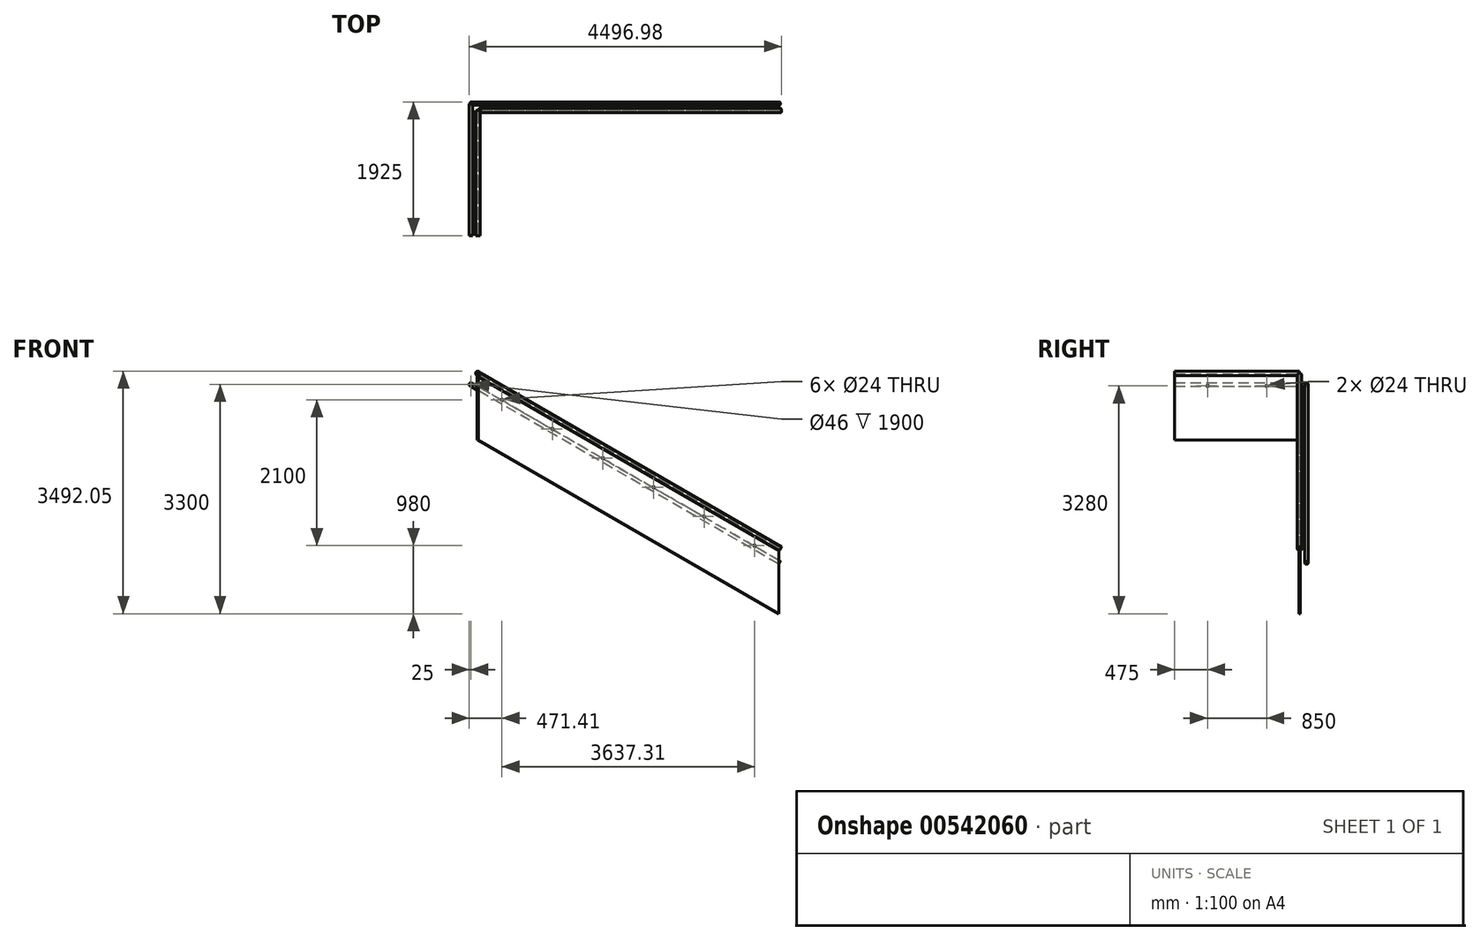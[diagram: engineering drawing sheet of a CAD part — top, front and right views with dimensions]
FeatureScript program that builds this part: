
annotation { "Feature Type Name" : "Feature", "Feature Type Description" : "" }
export const myFeature = defineFeature(function(context is Context, id is Id, definition is map)
    precondition{}
    {
        {
            var Q0;
            Q0=qCreatedBy(makeId("Front.planeOp"),FACE);
            var sketch = newSketch(context, id + "F0", { "sketchPlane" : qUnion([Q0])});
            skLineSegment(sketch, "E0", {"start": v(0, 0) * mm, "end": v(4330.13, -2500) * mm});
            skLineSegment(sketch, "E1", {"start": v(4330.13, -2500) * mm, "end": v(4330.13, -1550) * mm});
            skLineSegment(sketch, "E2", {"start": v(4330.13, -1550) * mm, "end": v(0, 950) * mm});
            skLineSegment(sketch, "E3.0", {"start": v(4330.13, -1720) * mm, "end": v(0, 780) * mm, "construction": true});
            skCircle(sketch, "E4", {"center": v(346.41, 580) * mm, "radius": 12 * mm});
            skCircle(sketch, "E5", {"center": v(3256.26, -1100) * mm, "radius": 12 * mm});
            skCircle(sketch, "E6", {"center": v(3983.72, -1520) * mm, "radius": 12 * mm});
            skCircle(sketch, "E7", {"center": v(1073.87, 160) * mm, "radius": 12 * mm});
            skCircle(sketch, "E8", {"center": v(1801.33, -260) * mm, "radius": 12 * mm});
            skCircle(sketch, "E9", {"center": v(2528.8, -680) * mm, "radius": 12 * mm});
            skLineSegment(sketch, "E10", {"start": v(0, 950) * mm, "end": v(0, 0) * mm});
            skSolve(sketch);
        }
        {
            var Q0;
            Q0=qSketchRegion(id+"F0",true);
            extrude(context, id + "F1", {"entities" : qUnion([Q0]), "endBound" : BoundingType.SYMMETRIC, "depth" : 19 * mm, "offsetDistance" : 25 * mm});
        }
        {
            var Q0;
            Q0=qCreatedBy(makeId("Right.planeOp"),FACE);
            var sketch = newSketch(context, id + "F2", { "sketchPlane" : qUnion([Q0])});
            skLineSegment(sketch, "E11.bottom", {"start": v(0, 950) * mm, "end": v(-1800, 950) * mm});
            skLineSegment(sketch, "E11.top", {"start": v(0, 0) * mm, "end": v(-1800, 0) * mm});
            skLineSegment(sketch, "E11.left", {"start": v(0, 950) * mm, "end": v(0, 0) * mm});
            skLineSegment(sketch, "E11.right", {"start": v(-1800, 950) * mm, "end": v(-1800, 0) * mm});
            skLineSegment(sketch, "E12", {"start": v(-1800, 780) * mm, "end": v(0, 780) * mm, "construction": true});
            skCircle(sketch, "E13", {"center": v(-1325, 780) * mm, "radius": 12 * mm});
            skCircle(sketch, "E14", {"center": v(-475, 780) * mm, "radius": 12 * mm});
            skSolve(sketch);
        }
        {
            var Q0;
            Q0=makeQuery(id+"F2.imprint","IMPRINT",FACE,{"disambiguationData":[TD([[makeQuery(id+"F2.imprint","IMPRINT",EDGE,{"derivedFrom":sQuery(id+"F2.wireOp",EDGE,"E11.bottom")}),1.0]])]});
            extrude(context, id + "F3", {"entities" : qUnion([Q0]), "operationType" : NewBodyOperationType.ADD, "endBound" : BoundingType.SYMMETRIC, "depth" : 19 * mm, "offsetDistance" : 25 * mm});
        }
        {
            var Q0;
            Q0=qCreatedBy(makeId("Front.planeOp"),FACE);
            var sketch = newSketch(context, id + "F4", { "sketchPlane" : qUnion([Q0])});
            skLineSegment(sketch, "E15.1", {"start": v(4356.1, -1565) * mm, "end": v(0, 950) * mm});
            skSolve(sketch);
        }
        {
            var Q0;
            Q0=qCreatedBy(makeId("Right.planeOp"),FACE);
            var sketch = newSketch(context, id + "F5", { "sketchPlane" : qUnion([Q0])});
            skLineSegment(sketch, "E16.0", {"start": v(0, 950) * mm, "end": v(-1800, 950) * mm});
            skSolve(sketch);
        }
        {
            var Q0;
            Q0=makeQuery(id+"F3.opExtrude","SWEPT_FACE",FACE,{"disambiguationData":[OSD([sQuery(id+"F2.wireOp",EDGE,"E11.right")])]});
            var sketch = newSketch(context, id + "F6", { "sketchPlane" : qUnion([Q0])});
            skLineSegment(sketch, "E17", {"start": v(9.5, 930) * mm, "end": v(9.5, 950) * mm});
            skLineSegment(sketch, "E18.0", {"start": v(-9.5, 950) * mm, "end": v(9.5, 950) * mm});
            skLineSegment(sketch, "E19", {"start": v(-9.5, 950) * mm, "end": v(-9.5, 930) * mm});
            skArc(sketch, "E20", {"start": v(9.5, 930) * mm, "mid": v(0, 992.05) * mm, "end": v(-9.5, 930) * mm});
            skArc(sketch, "E21.0", {"start": v(11, 932.12) * mm, "mid": v(0, 990.55) * mm, "end": v(-11, 932.12) * mm});
            skLineSegment(sketch, "E21.1", {"start": v(11, 932.12) * mm, "end": v(11, 951.5) * mm});
            skLineSegment(sketch, "E21.2", {"start": v(-11, 951.5) * mm, "end": v(11, 951.5) * mm});
            skLineSegment(sketch, "E21.3", {"start": v(-11, 951.5) * mm, "end": v(-11, 932.12) * mm});
            skSolve(sketch);
        }
        {
            var Q0;
            Q0=qSketchRegion(id+"F6",true);
            var Q1;
            Q1=sQuery(id+"F5.wireOp",EDGE,"E16.0");
            sweep(context, id + "F7", {"profiles" : qUnion([Q0]), "path" : qUnion([Q1])});
        }
        {
            var Q0;
            Q0=sQuery(id+"F4.wireOp",VERTEX,"E15.1.start");
            var Q1;
            Q1=sQuery(id+"F4.wireOp",EDGE,"E15.1");
            cPlane(context, id + "F8", {"entities" : qUnion([Q0, Q1]), "cplaneType" : CPlaneType.LINE_POINT, "offset" : 25 * mm, "width" : 150 * mm, "height" : 150 * mm});
        }
        {
            var Q0;
            Q0=qCreatedBy(id+"F8.planeOp",FACE);
            var sketch = newSketch(context, id + "F9", { "sketchPlane" : qUnion([Q0])});
            skLineSegment(sketch, "E22", {"start": v(10, 792.6) * mm, "end": v(10, 822.72) * mm});
            skLineSegment(sketch, "E23.0", {"start": v(-10, 822.72) * mm, "end": v(10, 822.72) * mm});
            skLineSegment(sketch, "E24", {"start": v(-10, 822.72) * mm, "end": v(-10, 792.6) * mm});
            skArc(sketch, "E25", {"start": v(10, 792.6) * mm, "mid": v(0, 854.47) * mm, "end": v(-10, 792.6) * mm});
            skArc(sketch, "E26.0", {"start": v(11.5, 794.75) * mm, "mid": v(0, 852.97) * mm, "end": v(-11.5, 794.75) * mm});
            skLineSegment(sketch, "E26.1", {"start": v(11.5, 794.75) * mm, "end": v(11.5, 824.22) * mm});
            skLineSegment(sketch, "E26.2", {"start": v(-11.5, 824.22) * mm, "end": v(11.5, 824.22) * mm});
            skLineSegment(sketch, "E26.3", {"start": v(-11.5, 824.22) * mm, "end": v(-11.5, 794.75) * mm});
            skSolve(sketch);
        }
        {
            var Q0;
            Q0=makeQuery(id+"F9.imprint","IMPRINT",FACE,{"disambiguationData":[TD([[makeQuery(id+"F9.imprint","IMPRINT",EDGE,{"derivedFrom":sQuery(id+"F9.wireOp",EDGE,"E22")}),-1.0]])]});
            var Q1;
            Q1=sQuery(id+"F0.wireOp",EDGE,"E2");
            sweep(context, id + "F10", {"profiles" : qUnion([Q0]), "path" : qUnion([Q1])});
        }
        {
            var Q0;
            Q0=makeQuery(id+"F7.opSweep","CAP_FACE",FACE,{"disambiguationData":[OSD([sQuery(id+"F4.wireOp",VERTEX,"E15.1.start"),sQuery(id+"F6.wireOp",EDGE,"E17"),sQuery(id+"F6.wireOp",EDGE,"E18.0"),sQuery(id+"F6.wireOp",EDGE,"E19"),sQuery(id+"F6.wireOp",EDGE,"E20"),sQuery(id+"F6.wireOp",EDGE,"E21.0"),sQuery(id+"F6.wireOp",EDGE,"E21.1"),sQuery(id+"F6.wireOp",EDGE,"E21.2"),sQuery(id+"F6.wireOp",EDGE,"E21.3")])],"isStart":false});
            var sketch = newSketch(context, id + "F11", { "sketchPlane" : qUnion([Q0])});
            skCircle(sketch, "E27", {"center": v(0, 960.3) * mm, "radius": 31.75 * mm});
            skSolve(sketch);
        }
        {
            var Q0;
            Q0=qSketchRegion(id+"F11",true);
            extrude(context, id + "F12", {"entities" : qUnion([Q0]), "operationType" : NewBodyOperationType.ADD, "oppositeDirection" : true, "depth" : 2 * mm, "offsetDistance" : 25 * mm});
        }
        {
            var Q0;
            Q0=qCreatedBy(makeId("Front.planeOp"),FACE);
            cPlane(context, id + "F13", {"entities" : qUnion([Q0]), "cplaneType" : CPlaneType.OFFSET, "offset" : 100 * mm, "oppositeDirection" : true, "width" : 150 * mm, "height" : 150 * mm});
        }
        {
            var Q0;
            Q0=qCreatedBy(id+"F13.planeOp",FACE);
            var sketch = newSketch(context, id + "F14", { "sketchPlane" : qUnion([Q0])});
            skLineSegment(sketch, "E28.0", {"start": v(4342.71, -1765) * mm, "end": v(-100, 800) * mm});
            skSolve(sketch);
        }
        {
            var Q0;
            Q0=sQuery(id+"F14.wireOp",EDGE,"E28.0");
            var Q1;
            Q1=sQuery(id+"F14.wireOp",VERTEX,"E28.0.start");
            cPlane(context, id + "F15", {"entities" : qUnion([Q0, Q1]), "cplaneType" : CPlaneType.LINE_POINT, "offset" : 25 * mm, "width" : 150 * mm, "height" : 150 * mm});
        }
        {
            var Q0;
            Q0=qCreatedBy(makeId("Top.planeOp"),FACE);
            cPlane(context, id + "F16", {"entities" : qUnion([Q0]), "cplaneType" : CPlaneType.OFFSET, "offset" : 800 * mm, "width" : 150 * mm, "height" : 150 * mm});
        }
        {
            var Q0;
            Q0=qCreatedBy(id+"F16.planeOp",FACE);
            var sketch = newSketch(context, id + "F17", { "sketchPlane" : qUnion([Q0])});
            skLineSegment(sketch, "E29", {"start": v(-100, 100) * mm, "end": v(-100, -1800) * mm});
            skSolve(sketch);
        }
        {
            var Q0;
            Q0=qCreatedBy(id+"F15.planeOp",FACE);
            var sketch = newSketch(context, id + "F18", { "sketchPlane" : qUnion([Q0])});
            skCircle(sketch, "E30", {"center": v(-100, 642.82) * mm, "radius": 25 * mm});
            skCircle(sketch, "E31.0", {"center": v(-100, 642.82) * mm, "radius": 23 * mm});
            skSolve(sketch);
        }
        {
            var Q0;
            Q0=makeQuery(id+"F18.imprint","IMPRINT",FACE,{"disambiguationData":[TD([[makeQuery(id+"F18.imprint","IMPRINT",EDGE,{"derivedFrom":sQuery(id+"F18.wireOp",EDGE,"E30")}),1.0]])]});
            var Q1;
            Q1=sQuery(id+"F14.wireOp",EDGE,"E28.0");
            sweep(context, id + "F19", {"profiles" : qUnion([Q0]), "path" : qUnion([Q1]), "keepProfileOrientation" : true});
        }
        {
            var Q0;
            Q0=sQuery(id+"F17.wireOp",EDGE,"E29");
            var Q1;
            Q1=sQuery(id+"F17.wireOp",VERTEX,"E29.end");
            cPlane(context, id + "F20", {"entities" : qUnion([Q0, Q1]), "cplaneType" : CPlaneType.LINE_POINT, "offset" : 25 * mm, "width" : 150 * mm, "height" : 150 * mm});
        }
        {
            var Q0;
            Q0=qCreatedBy(id+"F20.planeOp",FACE);
            var sketch = newSketch(context, id + "F21", { "sketchPlane" : qUnion([Q0])});
            skCircle(sketch, "E32", {"center": v(-100, 800) * mm, "radius": 25 * mm});
            skCircle(sketch, "E33.0", {"center": v(-100, 800) * mm, "radius": 23 * mm});
            skSolve(sketch);
        }
        {
            var Q0;
            Q0=makeQuery(id+"F21.imprint","IMPRINT",FACE,{"disambiguationData":[TD([[makeQuery(id+"F21.imprint","IMPRINT",EDGE,{"derivedFrom":sQuery(id+"F21.wireOp",EDGE,"E32")}),1.0]])]});
            var Q1;
            Q1=sQuery(id+"F17.wireOp",EDGE,"E29");
            sweep(context, id + "F22", {"operationType" : NewBodyOperationType.ADD, "profiles" : qUnion([Q0]), "path" : qUnion([Q1])});
        }
        {
            var Q0;
            Q0=makeQuery(id+"F19.opSweep","CAP_FACE",FACE,{"disambiguationData":[OSD([sQuery(id+"F14.wireOp",VERTEX,"E28.0.end"),sQuery(id+"F18.wireOp",EDGE,"E30"),sQuery(id+"F18.wireOp",EDGE,"E31.0")])],"isStart":false});
            var sketch = newSketch(context, id + "F23", { "sketchPlane" : qUnion([Q0])});
            skCircle(sketch, "E34", {"center": v(-100, 642.82) * mm, "radius": 25 * mm});
            skSolve(sketch);
        }
        {
            var Q0;
            Q0=qSketchRegion(id+"F23",true);
            extrude(context, id + "F24", {"entities" : qUnion([Q0]), "operationType" : NewBodyOperationType.ADD, "oppositeDirection" : true, "depth" : 3 * mm, "offsetDistance" : 25 * mm});
        }
        {
            var Q0;
            Q0=qCreatedBy(id+"F20.planeOp",FACE);
            var sketch = newSketch(context, id + "F25", { "sketchPlane" : qUnion([Q0])});
            skCircle(sketch, "E35.0", {"center": v(-100, 800) * mm, "radius": 25 * mm});
            skCircle(sketch, "E36.0", {"center": v(-100, 800) * mm, "radius": 40 * mm});
            skCircle(sketch, "E37", {"center": v(-100, 832.5) * mm, "radius": 4 * mm});
            skCircle(sketch, "E38", {"center": v(-71.85, 783.75) * mm, "radius": 4 * mm});
            skCircle(sketch, "E39", {"center": v(-128.15, 783.75) * mm, "radius": 4 * mm});
            skCircle(sketch, "E40", {"center": v(-100, 800) * mm, "radius": 32.5 * mm, "construction": true});
            skLineSegment(sketch, "E41", {"start": v(-100, 800) * mm, "end": v(-71.85, 783.75) * mm, "construction": true});
            skLineSegment(sketch, "E42", {"start": v(-100, 800) * mm, "end": v(-128.15, 783.75) * mm, "construction": true});
            skLineSegment(sketch, "E43", {"start": v(-100, 800) * mm, "end": v(-100, 832.5) * mm, "construction": true});
            skSolve(sketch);
        }
        {
            var Q0;
            Q0=makeQuery(id+"F25.imprint","IMPRINT",FACE,{"disambiguationData":[TD([[makeQuery(id+"F25.imprint","IMPRINT",EDGE,{"derivedFrom":sQuery(id+"F25.wireOp",EDGE,"E35.0")}),1.0]])]});
            extrude(context, id + "F26", {"entities" : qUnion([Q0]), "oppositeDirection" : true, "depth" : 5 * mm, "offsetDistance" : 25 * mm});
        }
    });
